# Revit family: Window-Hopper-Duratherm-Wood1
name_source: partatom
category: Windows
revit_build: Autodesk Revit 2013 (Build: 20121003_2115(x64)
units: mm (PartAtom-declared; Revit-internal decimal feet)

## types (1)
- 30" x 24"
    Air Leakage = 0.007
    Assembly Code = B2020130
    Default Sill Height = 3' - 0"
    Description = Wood hopper window with 1" insulated glazing. Contact manufacturer for customized needs.
    Design Pressure = DP60
    Desired Height = 2' - 0"
    Desired Width = 2' - 6"
    Energy Star Zone = N,NC,SC,S
    Glazing = Low E
    Glazing Opening Size SF = 2.49 SF
    Height = 2' - 0"
    LEED Credit = MR Credit 7
    Manufacturer = Duratherm Window Corporation
    Model = Hopper
    Operation = Hopper
    Product Documentation Link = http://www.durathermwindow.com
    R Value = 3.03
    Rough Height = 2' - 1"
    Rough Width = 2' - 7"
    Solar Heat Gain Coefficient = 0.38
    Style = Hopper
    Swing Open Distance = 8 5/8"
    Type Comments = 30" x 24" Hopper Wood Window with Lever Handle Operator
    U Value = 0.33
    URL = www.durathermwindow.com
    Visible Light Transmission = 0.7
    Wall Closure = By host
    Width = 2' - 6"

## geometry (parser evidence)
native form markers: Blend x14, Sweep x1
no freeform markers — native parametric forms only
